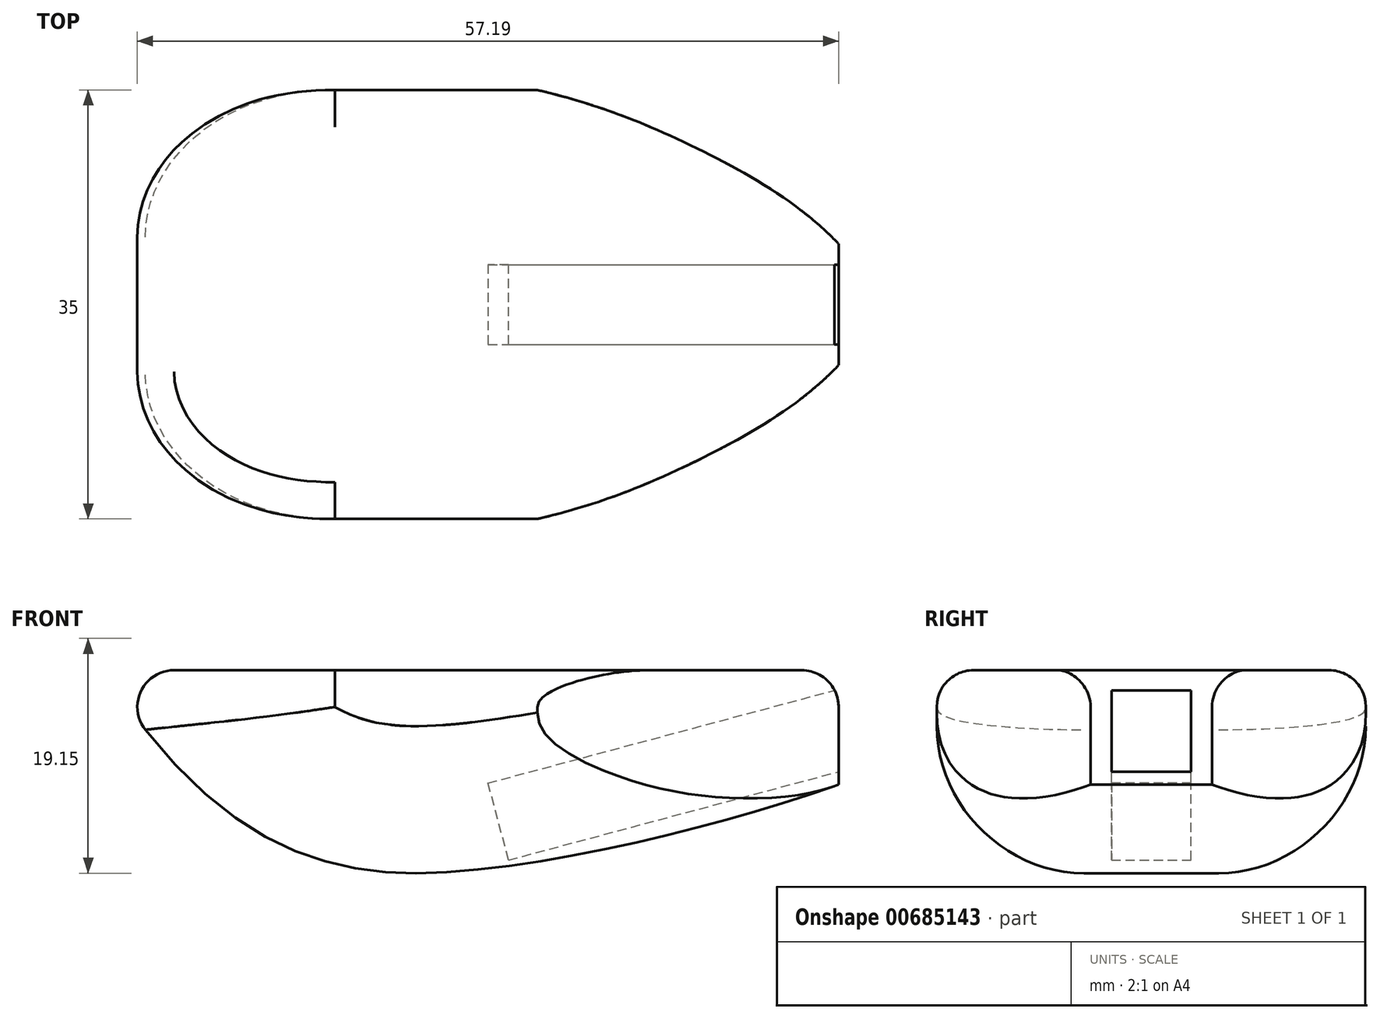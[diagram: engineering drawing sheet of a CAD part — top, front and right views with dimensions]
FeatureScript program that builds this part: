
annotation { "Feature Type Name" : "Feature", "Feature Type Description" : "" }
export const myFeature = defineFeature(function(context is Context, id is Id, definition is map)
    precondition{}
    {
        {
            var Q0;
            Q0=qCreatedBy(makeId("Front.planeOp"),FACE);
            var sketch = newSketch(context, id + "F0", { "sketchPlane" : qUnion([Q0])});
            skLineSegment(sketch, "E0.bottom", {"start": v(30, -11) * mm, "end": v(-30, -11) * mm});
            skLineSegment(sketch, "E0.top", {"start": v(30, 11) * mm, "end": v(-30, 11) * mm});
            skLineSegment(sketch, "E0.left", {"start": v(30, -11) * mm, "end": v(30, 11) * mm});
            skLineSegment(sketch, "E0.right", {"start": v(-30, -11) * mm, "end": v(-30, 11) * mm});
            skPoint(sketch, "E0.middle", {"position": v(0, 0) * mm});
            skFitSpline(sketch, "E1", {"points": [v(-30, 11) * mm, v(2.3, -5.07) * mm, v(30, 1.66) * mm], "startDerivative": vector(61.44, -95.42) * mm, "endDerivative": vector(45.3, 16.01) * mm});
            skSolve(sketch);
        }
        {
            var Q0;
            {var subQ0=sQuery(id+"F0.wireOp",EDGE,"E0.top");Q0=makeQuery(id+"F0.imprint","IMPRINT",FACE,{"disambiguationData":[TD([[makeQuery(id+"F0.imprint","IMPRINT",EDGE,{"derivedFrom":subQ0}),1.0]])]});}
            extrude(context, id + "F1", {"entities" : qUnion([Q0]), "endBound" : BoundingType.SYMMETRIC, "depth" : 35 * mm, "offsetDistance" : 25 * mm});
        }
        {
            var Q0;
            Q0=makeQuery(id+"F1.opExtrude","SWEPT_FACE",FACE,{"disambiguationData":[OSD([sQuery(id+"F0.wireOp",EDGE,"E0.left")])]});
            var Q1;
            Q1=makeQuery(id+"F1.opExtrude","SWEPT_EDGE",EDGE,{"disambiguationData":[OSD([sQuery(id+"F0.wireOp",EDGE,"E0.top"),sQuery(id+"F0.wireOp",EDGE,"E0.left")])]});
            cPlane(context, id + "F2", {"entities" : qUnion([Q0, Q1]), "cplaneType" : CPlaneType.LINE_ANGLE, "offset" : 25 * mm, "angle" : 15 * degree, "oppositeDirection" : true, "width" : 150 * mm, "height" : 150 * mm});
        }
        {
            var Q0;
            Q0=qCreatedBy(id+"F2.planeOp",FACE);
            var sketch = newSketch(context, id + "F3", { "sketchPlane" : qUnion([Q0])});
            skLineSegment(sketch, "E2", {"start": v(0, 1.36) * mm, "end": v(3.25, 1.36) * mm});
            skLineSegment(sketch, "E3", {"start": v(3.25, 1.36) * mm, "end": v(3.25, -5.14) * mm});
            skLineSegment(sketch, "E4", {"start": v(3.25, -5.14) * mm, "end": v(-3.25, -5.14) * mm});
            skLineSegment(sketch, "E5", {"start": v(-3.25, -5.14) * mm, "end": v(-3.25, 1.36) * mm});
            skLineSegment(sketch, "E6", {"start": v(-3.25, 1.36) * mm, "end": v(0, 1.36) * mm});
            skSolve(sketch);
        }
        {
            var Q0;
            Q0=makeQuery(id+"F3.imprint","IMPRINT",FACE,{"disambiguationData":[TD([[makeQuery(id+"F3.imprint","IMPRINT",EDGE,{"derivedFrom":sQuery(id+"F3.wireOp",EDGE,"E2")}),-1.0]])]});
            extrude(context, id + "F4", {"entities" : qUnion([Q0]), "operationType" : NewBodyOperationType.REMOVE, "depth" : 30 * mm, "offsetDistance" : 25 * mm});
        }
        {
            var Q0;
            Q0=makeQuery(id+"F1.opExtrude","SWEPT_FACE",FACE,{"disambiguationData":[OSD([sQuery(id+"F0.wireOp",EDGE,"E0.top")])]});
            var sketch = newSketch(context, id + "F5", { "sketchPlane" : qUnion([Q0])});
            skFitSpline(sketch, "E7", {"points": [v(5.43, 17.5) * mm, v(18.5, 12.72) * mm, v(30, 4.95) * mm], "startDerivative": vector(30.07, -7.03) * mm, "endDerivative": vector(18.93, -19.95) * mm});
            skFitSpline(sketch, "E8.MirrorCS", {"points": [v(5.43, -17.5) * mm, v(18.5, -12.72) * mm, v(30, -4.95) * mm], "startDerivative": vector(30.07, 7.03) * mm, "endDerivative": vector(18.93, 19.95) * mm});
            skSolve(sketch);
        }
        {
            var Q0;
            {var subQ0=sQuery(id+"F5.wireOp",EDGE,"E7");Q0=makeQuery(id+"F5.imprint","IMPRINT",FACE,{"disambiguationData":[TD([[makeQuery(id+"F5.imprint","IMPRINT",EDGE,{"derivedFrom":subQ0}),1.0]])]});}
            var Q1;
            {var subQ0=sQuery(id+"F5.wireOp",EDGE,"E8.MirrorCS");Q1=makeQuery(id+"F5.imprint","IMPRINT",FACE,{"disambiguationData":[TD([[makeQuery(id+"F5.imprint","IMPRINT",EDGE,{"derivedFrom":subQ0}),-1.0]])]});}
            extrude(context, id + "F6", {"entities" : qUnion([Q0, Q1]), "operationType" : NewBodyOperationType.REMOVE, "oppositeDirection" : true, "depth" : 25 * mm, "offsetDistance" : 25 * mm});
        }
        {
            var Q0;
            Q0=makeQuery(id+"F1.opExtrude","CAP_EDGE",EDGE,{"disambiguationData":[OSD([sQuery(id+"F0.wireOp",EDGE,"E1")])],"isStart":false});
            var Q1;
            Q1=makeQuery(id+"F1.opExtrude","CAP_EDGE",EDGE,{"disambiguationData":[OSD([sQuery(id+"F0.wireOp",EDGE,"E1")])],"isStart":true});
            fillet(context, id + "F7", {"entities" : qUnion([Q0, Q1]), "radius" : 12 * mm, "tangentPropagation" : true, "rho" : 0.4, "crossSection" : FilletCrossSection.CONIC, "allowEdgeOverflow" : false});
        }
        {
            var Q0;
            Q0=makeQuery(id+"F7.opFillet","BLEND_EDGE",EDGE,{"blendedFrom":[makeQuery(id+"F1.opExtrude","CAP_EDGE",EDGE,{"disambiguationData":[OSD([sQuery(id+"F0.wireOp",EDGE,"E1")])],"isStart":false}),makeQuery(id+"F1.opExtrude","SWEPT_FACE",FACE,{"disambiguationData":[OSD([sQuery(id+"F0.wireOp",EDGE,"E0.top")])]})],"blendedInto":[makeQuery(id+"F1.opExtrude","SWEPT_FACE",FACE,{"disambiguationData":[OSD([sQuery(id+"F0.wireOp",EDGE,"E0.top")])]})]});
            var Q1;
            Q1=makeQuery(id+"F7.opFillet","BLEND_EDGE",EDGE,{"blendedFrom":[makeQuery(id+"F1.opExtrude","CAP_EDGE",EDGE,{"disambiguationData":[OSD([sQuery(id+"F0.wireOp",EDGE,"E1")])],"isStart":true}),makeQuery(id+"F1.opExtrude","SWEPT_FACE",FACE,{"disambiguationData":[OSD([sQuery(id+"F0.wireOp",EDGE,"E0.top")])]})],"blendedInto":[makeQuery(id+"F1.opExtrude","SWEPT_FACE",FACE,{"disambiguationData":[OSD([sQuery(id+"F0.wireOp",EDGE,"E0.top")])]})]});
            var Q2;
            Q2=makeQuery(id+"F1.opExtrude","SWEPT_EDGE",EDGE,{"disambiguationData":[OSD([sQuery(id+"F0.wireOp",EDGE,"E0.top"),sQuery(id+"F0.wireOp",EDGE,"E0.right"),sQuery(id+"F0.wireOp",EDGE,"E1")])]});
            var Q3;
            Q3=makeQuery(id+"F6.boolean.opBoolean","COPY",EDGE,{"derivedFrom":makeQuery(id+"F6.opExtrude","CAP_EDGE",EDGE,{"disambiguationData":[OSD([sQuery(id+"F5.wireOp",EDGE,"E8.MirrorCS")])],"isStart":true})});
            var Q4;
            Q4=makeQuery(id+"F6.boolean.opBoolean","COPY",EDGE,{"derivedFrom":makeQuery(id+"F6.opExtrude","CAP_EDGE",EDGE,{"disambiguationData":[OSD([sQuery(id+"F5.wireOp",EDGE,"E7")])],"isStart":true})});
            var Q5;
            Q5=makeQuery(id+"F1.opExtrude","CAP_EDGE",EDGE,{"disambiguationData":[OSD([sQuery(id+"F0.wireOp",EDGE,"E0.top")])],"isStart":false});
            var Q6;
            Q6=makeQuery(id+"F1.opExtrude","CAP_EDGE",EDGE,{"disambiguationData":[OSD([sQuery(id+"F0.wireOp",EDGE,"E0.top")])],"isStart":true});
            fillet(context, id + "F8", {"entities" : qUnion([Q0, Q1, Q2, Q3, Q4, Q5, Q6]), "radius" : 3 * mm, "tangentPropagation" : true, "allowEdgeOverflow" : false});
        }
        {
            var Q0;
            Q0=makeQuery(id+"F6.boolean.opBoolean","COPY",EDGE,{"derivedFrom":makeQuery(id+"F6.opExtrude","SWEPT_EDGE",EDGE,{"disambiguationData":[OSD([sQuery(id+"F0.wireOp",EDGE,"E0.top"),sQuery(id+"F0.wireOp",EDGE,"E0.left"),sQuery(id+"F5.wireOp",EDGE,"E7")])]})});
            var Q1;
            Q1=makeQuery(id+"F7.opFillet","BLEND_EDGE",EDGE,{"blendedFrom":[makeQuery(id+"F1.opExtrude","CAP_EDGE",EDGE,{"disambiguationData":[OSD([sQuery(id+"F0.wireOp",EDGE,"E1")])],"isStart":true}),makeQuery(id+"F1.opExtrude","SWEPT_FACE",FACE,{"disambiguationData":[OSD([sQuery(id+"F0.wireOp",EDGE,"E0.left")])]})],"blendedInto":[makeQuery(id+"F1.opExtrude","SWEPT_FACE",FACE,{"disambiguationData":[OSD([sQuery(id+"F0.wireOp",EDGE,"E0.left")])]})]});
            var Q2;
            Q2=makeQuery(id+"F7.opFillet","BLEND_EDGE",EDGE,{"blendedFrom":[makeQuery(id+"F1.opExtrude","CAP_EDGE",EDGE,{"disambiguationData":[OSD([sQuery(id+"F0.wireOp",EDGE,"E1")])],"isStart":false}),makeQuery(id+"F1.opExtrude","SWEPT_FACE",FACE,{"disambiguationData":[OSD([sQuery(id+"F0.wireOp",EDGE,"E0.left")])]})],"blendedInto":[makeQuery(id+"F1.opExtrude","SWEPT_FACE",FACE,{"disambiguationData":[OSD([sQuery(id+"F0.wireOp",EDGE,"E0.left")])]})]});
            var Q3;
            Q3=makeQuery(id+"F6.boolean.opBoolean","COPY",EDGE,{"derivedFrom":makeQuery(id+"F6.opExtrude","SWEPT_EDGE",EDGE,{"disambiguationData":[OSD([sQuery(id+"F0.wireOp",EDGE,"E0.top"),sQuery(id+"F0.wireOp",EDGE,"E0.left"),sQuery(id+"F5.wireOp",EDGE,"E8.MirrorCS")])]})});
            var Q4;
            Q4=makeQuery(id+"F8.opFillet","BLEND_EDGE",EDGE,{"blendedFrom":[makeQuery(id+"F6.boolean.opBoolean","COPY",EDGE,{"derivedFrom":makeQuery(id+"F6.opExtrude","CAP_EDGE",EDGE,{"disambiguationData":[OSD([sQuery(id+"F5.wireOp",EDGE,"E7")])],"isStart":true})}),makeQuery(id+"F1.opExtrude","SWEPT_FACE",FACE,{"disambiguationData":[OSD([sQuery(id+"F0.wireOp",EDGE,"E0.left")])]})],"blendedInto":[makeQuery(id+"F1.opExtrude","SWEPT_FACE",FACE,{"disambiguationData":[OSD([sQuery(id+"F0.wireOp",EDGE,"E0.left")])]})]});
            var Q5;
            Q5=makeQuery(id+"F8.opFillet","BLEND_EDGE",EDGE,{"blendedFrom":[makeQuery(id+"F6.boolean.opBoolean","COPY",EDGE,{"derivedFrom":makeQuery(id+"F6.opExtrude","CAP_EDGE",EDGE,{"disambiguationData":[OSD([sQuery(id+"F5.wireOp",EDGE,"E8.MirrorCS")])],"isStart":true})}),makeQuery(id+"F1.opExtrude","SWEPT_FACE",FACE,{"disambiguationData":[OSD([sQuery(id+"F0.wireOp",EDGE,"E0.left")])]})],"blendedInto":[makeQuery(id+"F1.opExtrude","SWEPT_FACE",FACE,{"disambiguationData":[OSD([sQuery(id+"F0.wireOp",EDGE,"E0.left")])]})]});
            var Q6;
            Q6=makeQuery(id+"F1.opExtrude","SWEPT_EDGE",EDGE,{"disambiguationData":[OSD([sQuery(id+"F0.wireOp",EDGE,"E0.top"),sQuery(id+"F0.wireOp",EDGE,"E0.left")])]});
            fillet(context, id + "F9", {"entities" : qUnion([Q0, Q1, Q2, Q3, Q4, Q5, Q6]), "radius" : 3 * mm, "tangentPropagation" : true, "allowEdgeOverflow" : false});
        }
        {
            var Q0;
            Q0=makeQuery(id+"F4.boolean.opBoolean","COPY",EDGE,{"derivedFrom":makeQuery(id+"F4.opExtrude","CAP_EDGE",EDGE,{"disambiguationData":[OSD([sQuery(id+"F3.wireOp",EDGE,"E2"),sQuery(id+"F3.wireOp",EDGE,"E6")])],"isStart":false})});
            var Q1;
            Q1=makeQuery(id+"F4.boolean.opBoolean","COPY",VERTEX,{"derivedFrom":makeQuery(id+"F4.opExtrude","CAP_VERTEX",VERTEX,{"disambiguationData":[OSD([sQuery(id+"F3.wireOp",EDGE,"E4"),sQuery(id+"F3.wireOp",EDGE,"E5")])],"isStart":false})});
            cPlane(context, id + "F10", {"entities" : qUnion([Q0, Q1]), "cplaneType" : CPlaneType.LINE_ANGLE, "offset" : 25 * mm, "angle" : 50 * degree, "oppositeDirection" : true, "width" : 150 * mm, "height" : 150 * mm});
        }
    });
